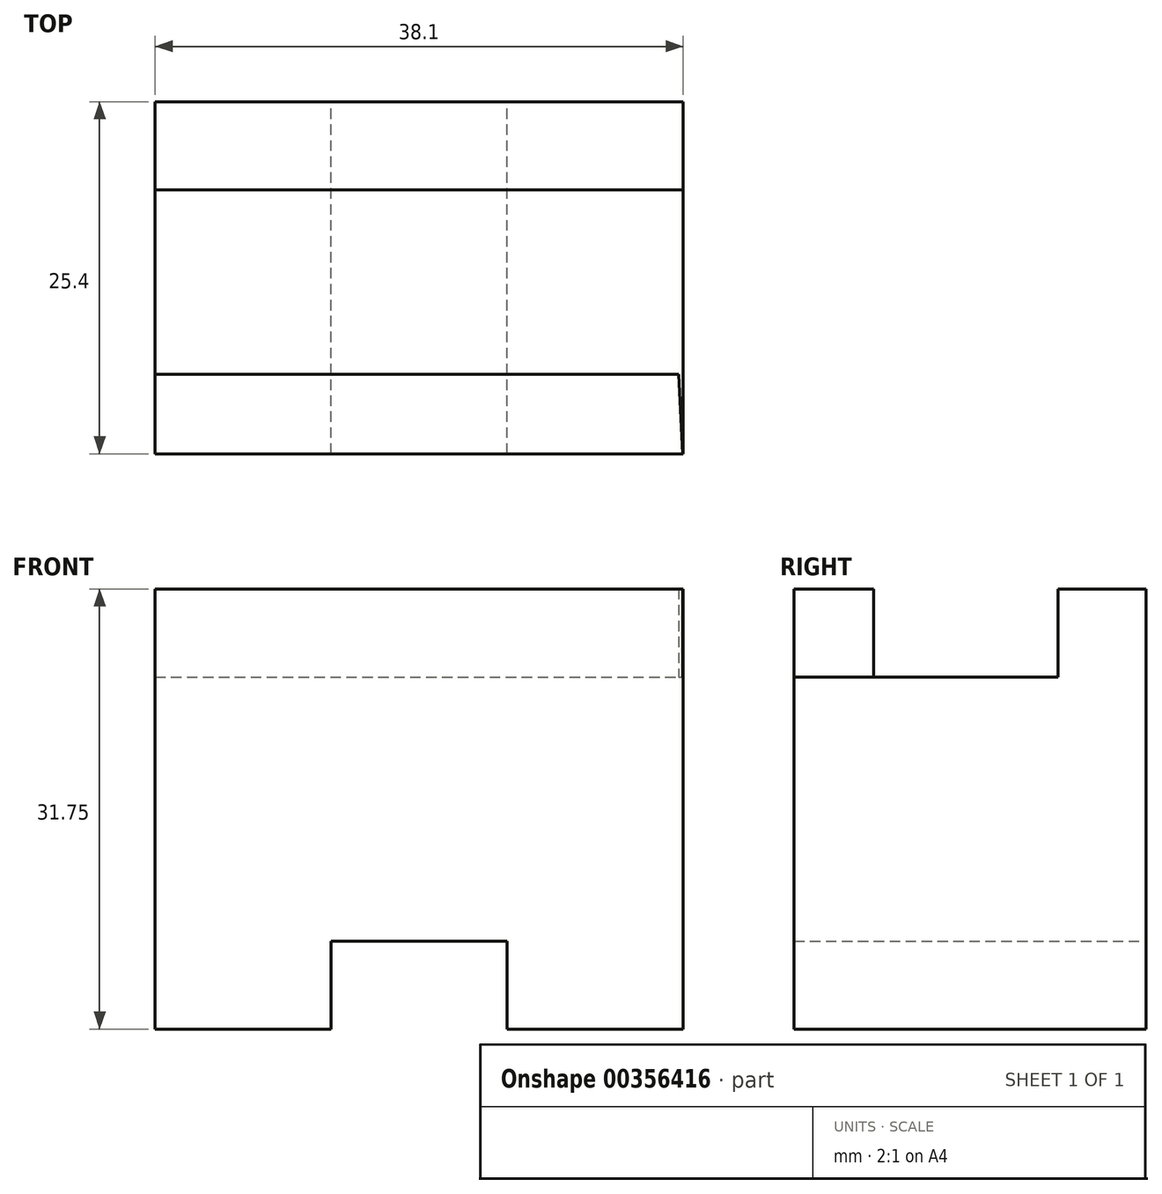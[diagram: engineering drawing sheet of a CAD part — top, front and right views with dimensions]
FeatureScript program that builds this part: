
annotation { "Feature Type Name" : "Feature", "Feature Type Description" : "" }
export const myFeature = defineFeature(function(context is Context, id is Id, definition is map)
    precondition{}
    {
        {
            var Q0;
            Q0=qCreatedBy(makeId("Front.planeOp"),FACE);
            var sketch = newSketch(context, id + "F0", { "sketchPlane" : qUnion([Q0])});
            skLineSegment(sketch, "E0", {"start": v(0, 25.4) * mm, "end": v(0, 0) * mm});
            skLineSegment(sketch, "E1", {"start": v(0, 0) * mm, "end": v(12.7, 0) * mm});
            skLineSegment(sketch, "E2", {"start": v(12.7, 0) * mm, "end": v(12.7, 6.35) * mm});
            skLineSegment(sketch, "E3", {"start": v(12.7, 6.35) * mm, "end": v(25.4, 6.35) * mm});
            skLineSegment(sketch, "E4", {"start": v(25.4, 6.35) * mm, "end": v(25.4, 0) * mm});
            skLineSegment(sketch, "E5", {"start": v(25.4, 0) * mm, "end": v(38.1, 0) * mm});
            skLineSegment(sketch, "E6", {"start": v(0, 25.4) * mm, "end": v(38.1, 25.4) * mm});
            skLineSegment(sketch, "E7", {"start": v(38.1, 25.4) * mm, "end": v(38.1, 0) * mm});
            skSolve(sketch);
        }
        {
            var Q0;
            Q0 = qSketchRegion(id + "F0", true);
            extrude(context, id + "F1", {"entities" : qUnion([Q0]), "depth" : 25.4 * mm});
        }
        {
            var Q0;
            Q0=makeQuery(id+"F1.opExtrude","SWEPT_FACE",FACE,{"disambiguationData":[OSD([sQuery(id+"F0.wireOp",EDGE,"E6")])]});
            var sketch = newSketch(context, id + "F2", { "sketchPlane" : qUnion([Q0])});
            skSolve(sketch);
        }
        {
            var Q0;
            {var subQ0=sQuery(id+"F0.wireOp",EDGE,"E6");Q0=makeQuery(id+"F2.imprint","IMPRINT",FACE,{"disambiguationData":[TD([[makeQuery(id+"F2.imprint","IMPRINT",EDGE,{"derivedFrom":makeQuery(id+"F1.opExtrude","CAP_EDGE",EDGE,{"disambiguationData":[OSD([subQ0])],"isStart":true})}),-1.0]])]});}
            var sketch = newSketch(context, id + "F3", { "sketchPlane" : qUnion([Q0])});
            skLineSegment(sketch, "E8", {"start": v(0, 0) * mm, "end": v(0, -6.35) * mm});
            skLineSegment(sketch, "E9", {"start": v(0, -6.35) * mm, "end": v(38.1, -6.35) * mm});
            skLineSegment(sketch, "E10", {"start": v(38.1, -6.35) * mm, "end": v(38.1, 0) * mm});
            skLineSegment(sketch, "E11", {"start": v(38.1, 0) * mm, "end": v(0, 0) * mm});
            skSolve(sketch);
        }
        {
            var Q0;
            Q0 = qSketchRegion(id + "F3", true);
            extrude(context, id + "F4", {"entities" : qUnion([Q0]), "operationType" : NewBodyOperationType.ADD, "depth" : 6.35 * mm});
        }
        {
            var Q0;
            {var subQ0=sQuery(id+"F0.wireOp",EDGE,"E6");Q0=makeQuery(id+"F2.imprint","IMPRINT",FACE,{"disambiguationData":[TD([[makeQuery(id+"F2.imprint","IMPRINT",EDGE,{"derivedFrom":makeQuery(id+"F1.opExtrude","CAP_EDGE",EDGE,{"disambiguationData":[OSD([subQ0])],"isStart":true})}),-1.0]])]});}
            var sketch = newSketch(context, id + "F5", { "sketchPlane" : qUnion([Q0])});
            skLineSegment(sketch, "E12", {"start": v(0, -19.65) * mm, "end": v(0, -25.54) * mm});
            skLineSegment(sketch, "E13", {"start": v(0, -25.54) * mm, "end": v(38.07, -25.54) * mm});
            skLineSegment(sketch, "E14", {"start": v(0, -19.65) * mm, "end": v(37.76, -19.65) * mm});
            skLineSegment(sketch, "E15", {"start": v(37.76, -19.65) * mm, "end": v(38.07, -25.54) * mm});
            skSolve(sketch);
        }
        {
            var Q0;
            {var subQ4=sQuery(id+"F5.wireOp",EDGE,"E14");Q0=makeQuery(id+"F5.imprint","IMPRINT",FACE,{"disambiguationData":[TD([[makeQuery(id+"F5.imprint","IMPRINT",EDGE,{"derivedFrom":subQ4}),-1.0]])]});}
            extrude(context, id + "F6", {"entities" : qUnion([Q0]), "operationType" : NewBodyOperationType.ADD, "depth" : 6.35 * mm});
        }
    });
